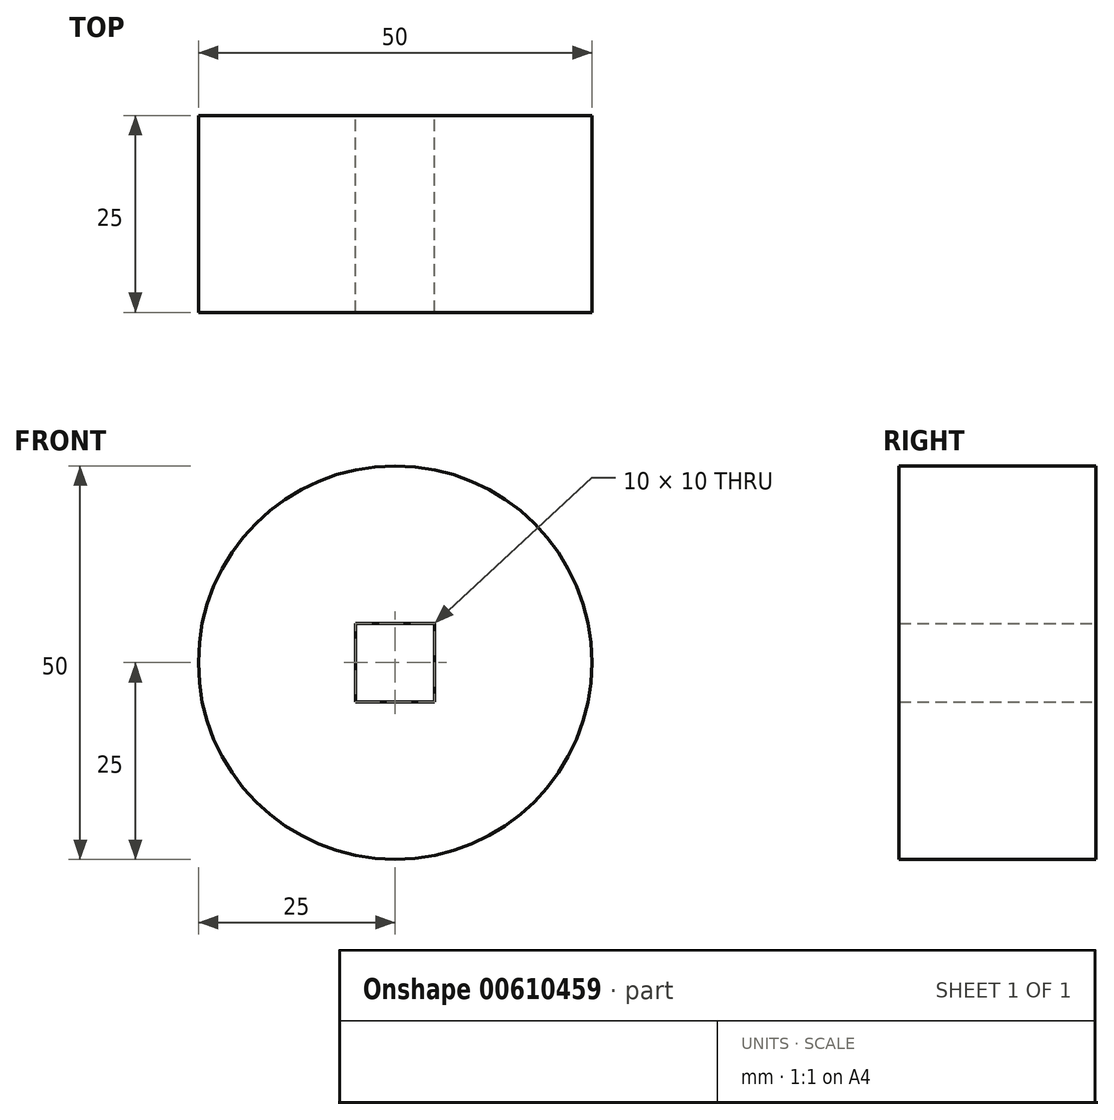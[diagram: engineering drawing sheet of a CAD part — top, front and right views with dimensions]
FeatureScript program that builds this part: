
annotation { "Feature Type Name" : "Feature", "Feature Type Description" : "" }
export const myFeature = defineFeature(function(context is Context, id is Id, definition is map)
    precondition{}
    {
        {
            var Q0;
            Q0=qCreatedBy(makeId("Front.planeOp"),FACE);
            var sketch = newSketch(context, id + "F0", { "sketchPlane" : qUnion([Q0])});
            skCircle(sketch, "E0", {"center": v(0, 0) * mm, "radius": 25 * mm});
            skLineSegment(sketch, "E1.bottom", {"start": v(5, -5) * mm, "end": v(-5, -5) * mm});
            skLineSegment(sketch, "E1.top", {"start": v(5, 5) * mm, "end": v(-5, 5) * mm});
            skLineSegment(sketch, "E1.left", {"start": v(5, -5) * mm, "end": v(5, 5) * mm});
            skLineSegment(sketch, "E1.right", {"start": v(-5, -5) * mm, "end": v(-5, 5) * mm});
            skSolve(sketch);
        }
        {
            var Q0;
            Q0 = qBodyType(qCreatedBy(id + "F0" ,EDGE), BodyType.WIRE);
            var Q1;
            Q1=sQuery(id+"F0.wireOp",EDGE,"E0");
            extrude(context, id + "F1", {"bodyType" : ToolBodyType.SURFACE, "surfaceEntities" : qUnion([Q0, Q1]), "depth" : 50 * mm, "offsetDistance" : 25 * mm});
        }
        {
            var Q0;
            Q0=makeQuery(id+"F0.imprint","IMPRINT",FACE,{"disambiguationData":[TD([[makeQuery(id+"F0.imprint","IMPRINT",EDGE,{"derivedFrom":sQuery(id+"F0.wireOp",EDGE,"E0")}),1.0]])]});
            extrude(context, id + "F2", {"entities" : qUnion([Q0]), "depth" : 25 * mm, "offsetDistance" : 25 * mm});
        }
    });
